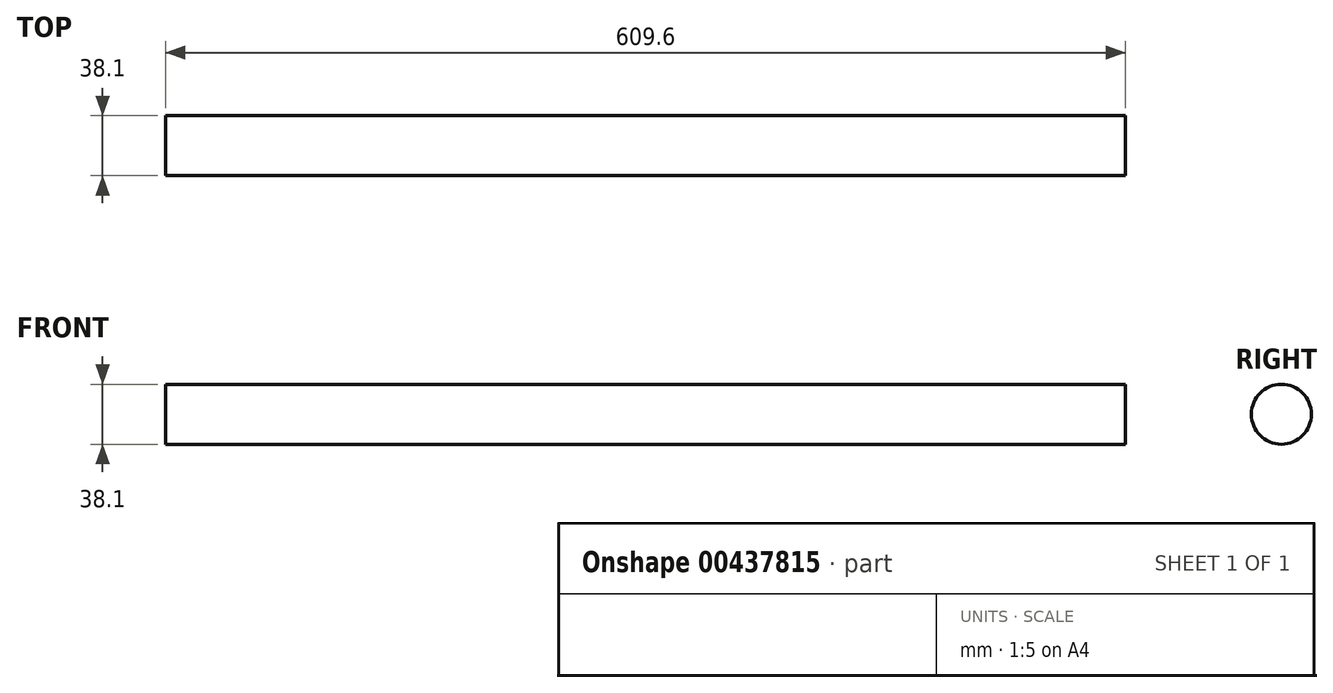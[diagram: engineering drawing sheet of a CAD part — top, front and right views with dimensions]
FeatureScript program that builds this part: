
annotation { "Feature Type Name" : "Feature", "Feature Type Description" : "" }
export const myFeature = defineFeature(function(context is Context, id is Id, definition is map)
    precondition{}
    {
        {
            var Q0;
            Q0=qCreatedBy(makeId("Right.planeOp"),FACE);
            var sketch = newSketch(context, id + "F0", { "sketchPlane" : qUnion([Q0])});
            skCircle(sketch, "E0", {"center": v(0, 0) * mm, "radius": 19.05 * mm});
            skSolve(sketch);
        }
        {
            var Q0;
            Q0=makeQuery(id+"F0.imprint","IMPRINT",FACE,{"disambiguationData":[TD([[makeQuery(id+"F0.imprint","IMPRINT",EDGE,{"derivedFrom":sQuery(id+"F0.wireOp",EDGE,"E0")}),1.0]])]});
            extrude(context, id + "F1", {"entities" : qUnion([Q0]), "depth" : 609.6 * mm});
        }
    });
